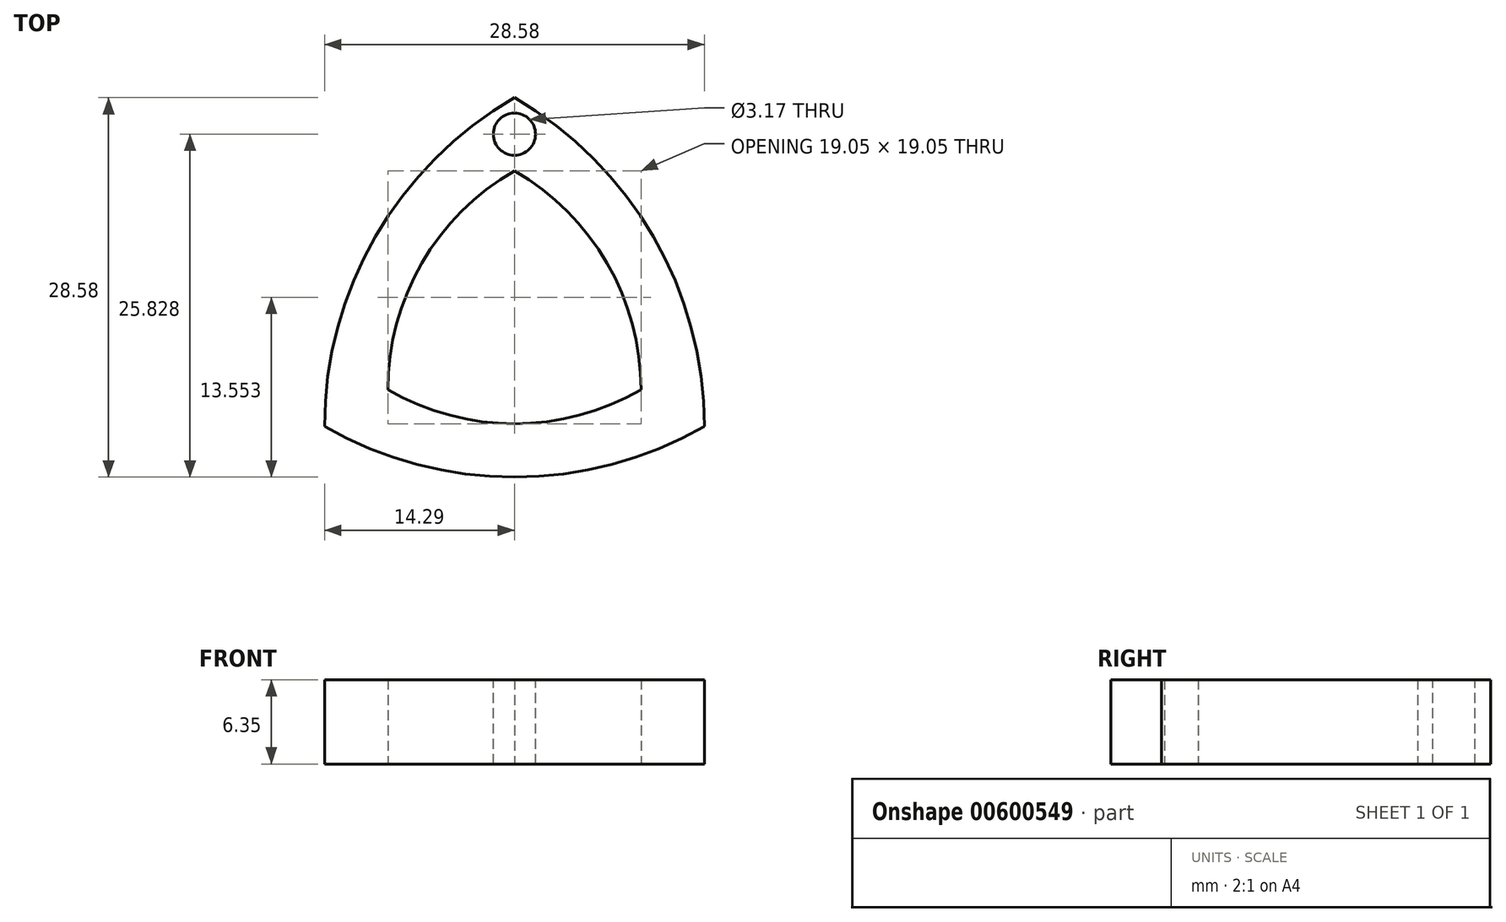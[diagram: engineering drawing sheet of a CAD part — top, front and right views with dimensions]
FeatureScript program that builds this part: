
annotation { "Feature Type Name" : "Feature", "Feature Type Description" : "" }
export const myFeature = defineFeature(function(context is Context, id is Id, definition is map)
    precondition{}
    {
        {
            var Q0;
            Q0=qCreatedBy(makeId("Top.planeOp"),FACE);
            var sketch = newSketch(context, id + "F0", { "sketchPlane" : qUnion([Q0])});
            skCircle(sketch, "E0.cCircle", {"center": v(0, 0) * mm, "radius": 5.5 * mm, "construction": true});
            skLineSegment(sketch, "E0.0", {"start": v(0, 11) * mm, "end": v(9.53, -5.5) * mm, "construction": true});
            skLineSegment(sketch, "E0.1", {"start": v(9.53, -5.5) * mm, "end": v(-9.53, -5.5) * mm, "construction": true});
            skLineSegment(sketch, "E0.2", {"start": v(-9.53, -5.5) * mm, "end": v(0, 11) * mm, "construction": true});
            skArc(sketch, "E1", {"start": v(0, 11) * mm, "mid": v(-6.97, 4.03) * mm, "end": v(-9.52, -5.5) * mm});
            skArc(sketch, "E2", {"start": v(9.53, -5.5) * mm, "mid": v(6.97, 4.03) * mm, "end": v(0, 11) * mm});
            skArc(sketch, "E3", {"start": v(-9.53, -5.5) * mm, "mid": v(0, -8.05) * mm, "end": v(9.53, -5.5) * mm});
            skSolve(sketch);
        }
        {
            var Q0;
            Q0=qCreatedBy(makeId("Top.planeOp"),FACE);
            var sketch = newSketch(context, id + "F1", { "sketchPlane" : qUnion([Q0])});
            skCircle(sketch, "E4.cCircle", {"center": v(0, 0) * mm, "radius": 8.25 * mm, "construction": true});
            skLineSegment(sketch, "E4.0", {"start": v(0, 16.5) * mm, "end": v(14.29, -8.25) * mm, "construction": true});
            skLineSegment(sketch, "E4.1", {"start": v(14.29, -8.25) * mm, "end": v(-14.29, -8.25) * mm, "construction": true});
            skLineSegment(sketch, "E4.2", {"start": v(-14.29, -8.25) * mm, "end": v(0, 16.5) * mm, "construction": true});
            skPoint(sketch, "E4.0.midPoint", {"position": v(7.14, 4.12) * mm});
            skArc(sketch, "E5", {"start": v(0, 16.5) * mm, "mid": v(-10.46, 6.04) * mm, "end": v(-14.29, -8.25) * mm});
            skArc(sketch, "E6", {"start": v(14.29, -8.25) * mm, "mid": v(10.46, 6.04) * mm, "end": v(0, 16.5) * mm});
            skArc(sketch, "E7", {"start": v(-14.29, -8.25) * mm, "mid": v(0, -12.08) * mm, "end": v(14.29, -8.25) * mm});
            skSolve(sketch);
        }
        {
            var Q0;
            Q0 = qSketchRegion(id + "F1", true);
            extrude(context, id + "F2", {"entities" : qUnion([Q0]), "depth" : 6.35 * mm, "offsetDistance" : 25.4 * mm});
        }
        {
            var Q0;
            Q0 = qSketchRegion(id + "F0", true);
            var Q1;
            Q1=makeQuery(id+"F2.opExtrude","CAP_FACE",FACE,{"disambiguationData":[OSD([sQuery(id+"F1.wireOp",EDGE,"E5"),sQuery(id+"F1.wireOp",EDGE,"E6"),sQuery(id+"F1.wireOp",EDGE,"E7")])],"isStart":false});
            extrude(context, id + "F3", {"entities" : qUnion([Q0]), "operationType" : NewBodyOperationType.REMOVE, "endBound" : BoundingType.UP_TO_SURFACE, "depth" : 25.4 * mm, "endBoundEntityFace" : qUnion([Q1]), "offsetDistance" : 25.4 * mm});
        }
        {
            var Q0;
            Q0=makeQuery(id+"F2.opExtrude","CAP_FACE",FACE,{"disambiguationData":[OSD([sQuery(id+"F1.wireOp",EDGE,"E5"),sQuery(id+"F1.wireOp",EDGE,"E6"),sQuery(id+"F1.wireOp",EDGE,"E7")])],"isStart":false});
            var sketch = newSketch(context, id + "F4", { "sketchPlane" : qUnion([Q0])});
            skCircle(sketch, "E8", {"center": v(0, 13.75) * mm, "radius": 1.59 * mm});
            skLineSegment(sketch, "E9", {"start": v(0, 16.5) * mm, "end": v(0, 11) * mm, "construction": true});
            skSolve(sketch);
        }
        {
            var Q0;
            Q0 = qSketchRegion(id + "F4", true);
            extrude(context, id + "F5", {"entities" : qUnion([Q0]), "operationType" : NewBodyOperationType.REMOVE, "oppositeDirection" : true, "depth" : 6.45 * mm, "offsetDistance" : 25.4 * mm});
        }
    });
